# Revit family: IS_iLifeS_T4593_BIM_GB
name_source: partatom
category: Plumbing Fixtures
units: mm (PartAtom-declared; Revit-internal decimal feet)

## family parameters
Always vertical = No
Cut with Voids When Loaded = No
OmniClass Number = 23.45.05.14.27
OmniClass Title = Bidets
Part Type = Normal
Room Calculation Point = No
Round Connector Dimension = Use Diameter
Shared = No
Work Plane-Based = No

## types (2) — shared parameters
Accessories = https://www.idealstandard.co.uk
AreaUnits = millimetres
AssetType = Fixed
BIMObjectName = IS_IdealStandard_Bidets_i.lifeS_T4593
BIMobject category = Bidets
BIMobject category code = sanitary-bidets
BIMobject main category = Sanitary
BIMobject main category code = sanitary
BidetMounting = Wall Hung Bidet
Brand = Ideal Standard
Brand url = http://www.idealstandard.co.uk
Category = Sanitary
ConnectionType = Plumbing
CurrencyUnit = £
CurrentRevision = 1
Date of publishing = 27/05/2022
DurationUnit = Years
Edition number = 1
ElementType = Fixed
ExpectedLife = 99
Help = https://www.idealstandard.co.uk
IFC Classification = Sanitary Terminal
IfcExportAs = IfcSanitaryTerminalType
IfcExportType = TOILETPAN
Installation instructions = https://www.idealstandard.co.uk
InstallationInstructions = https://www.idealstandard.co.uk
LinearUnits = Millimetres
MaintenanceInformation = https://www.idealstandard.co.uk
Manufacturer = Ideal Standard
Manufacturer name = Ideal Standard
ManufacturerURL = https://www.idealstandard.co.uk
Material = Vitrous China
Material main = Vitrous China
ModelReference = i.life S wallhung bidet
NBS Reference Code = 45-35-70/320
NBS Reference Description = Bidets
Name = Bidets_i.lifeS_T4593_IdealStandard
NettWeight = 17.55
NominalDepth = 480 mm
NominalHeight = 298 mm
NominalLength = 480 mm
NominalWidth = 353 mm
OmniClass Code = 23-31 23 00
OmniClass Description = Bidest
PredefinedType = Sanitary
Product Guid = 7b4bc57b-5069-4884-a7bc-7c1feb318dc5
Product SKU = T4593
Product certification = https://www.idealstandard.co.uk
Product data url = https://bimobject.com
Product family = I.life S
Product group = Saniatry : Bidets
Product name = i.life S wallhung bidet
Product url = https://www.idealstandard.co.uk
ProductInformation = https://www.idealstandard.co.uk
QR code = http://bimobject.com
ReplacementCost = 0
Shape = Sculpture
Size = 480 x 300 x 355 mm
Space = Internal
SpareParts = https://www.idealstandard.co.uk
Technical description = https://www.idealstandard.co.uk
UNSPSC Code = 301815
URL = https://www.idealstandard.co.uk
Uniclass 2015 Code = Pr_40_20_06_11
Uniclass 2015 Name = Bidets
Uniclass2015Code = Pr_40_20_06_11
Uniclass2015Title = Bidets
Uniclass2015Version = v.25
Version = 1
VolumeUnits = Litres
WRASURL = https://www.wrasapprovals.co.uk
WarrantyDescription = manufacturer warranty
WarrantyDurationUnit = years
Youtube clip = https://www.youtube.com
zero-valued in all types: Cost

## per-type parameters (varying)
| type | BarCode | Color | Description | Features | Finish | GTIN code | MainColor | Model | ModelNumber |
| T459301 - i.life S wallhung bidet - White | 8014140491743 | White | Ideal Standard i.life S wallhung bidet, compact, hidden fixation, overflow round, white, in carton box, EU pallet | wallhung bidet, compact, hidden fixation, overflow round, white, in carton box, EU pallet | White | https://8014140491743 | White | T459301 | T459301 |
| T4593MA - i.life S wallhung bidet - Ideal Plus White | 8014140491750 | Ideal Plus White | Ideal Standard i.life S wallhung bidet, compact, hidden fixation, overflow round, white Ideal PLus, in carton box, EU pallet | wallhung bidet, compact, hidden fixation, overflow round, white Ideal PLus, in carton box, EU pallet | Ideal Plus White | https://8014140491750 | Ideal Plus White | T4593MA | T4593MA |

## geometry (parser evidence)
native form markers: Sweep x2
no freeform markers — native parametric forms only
